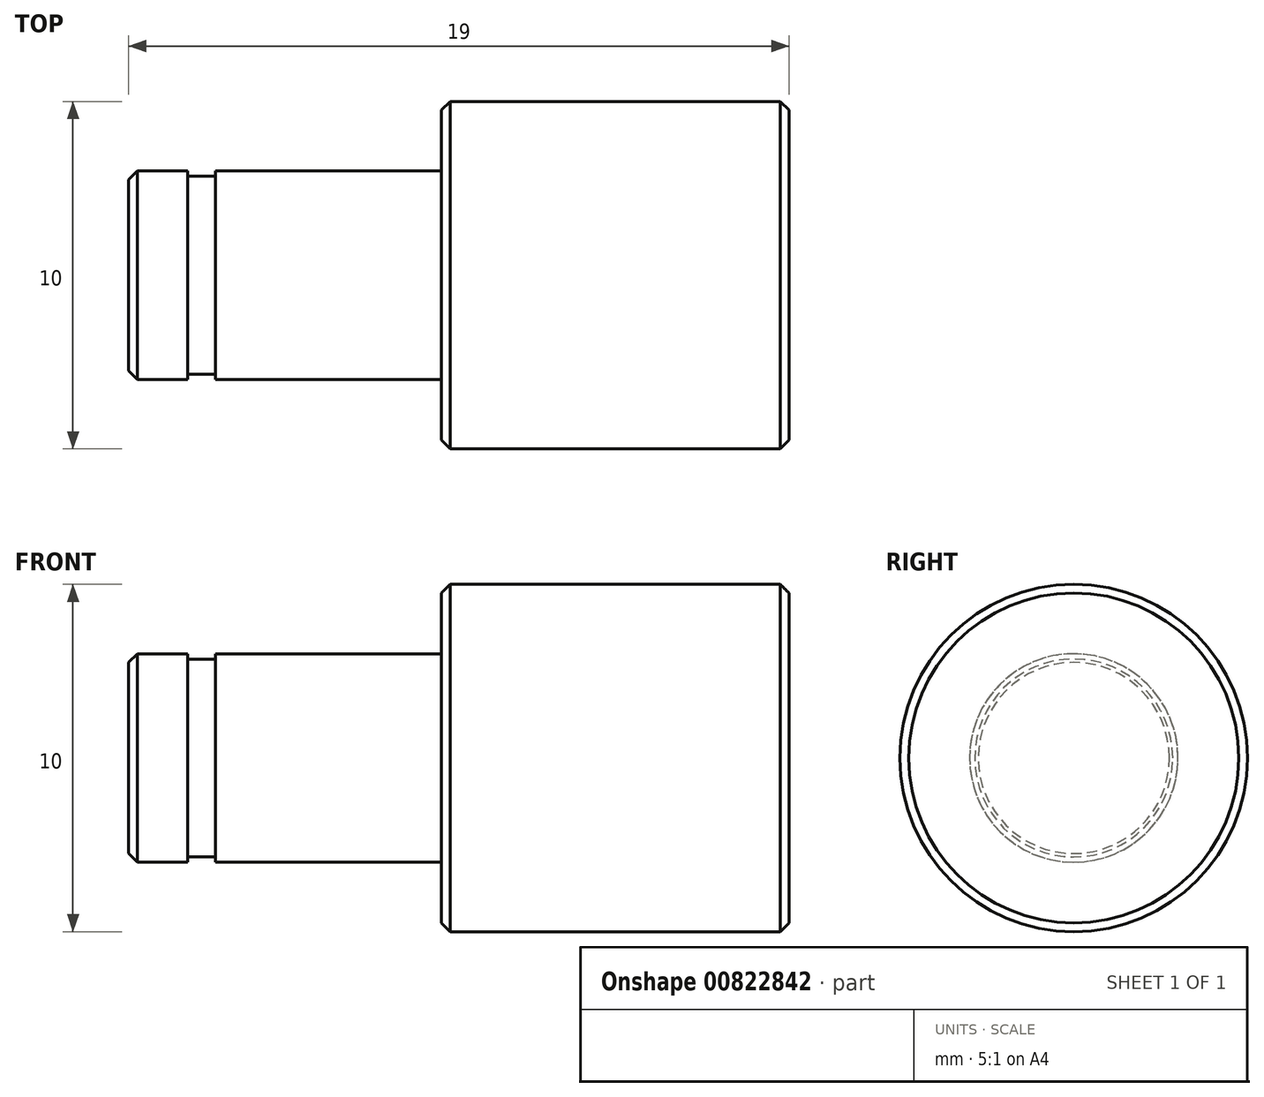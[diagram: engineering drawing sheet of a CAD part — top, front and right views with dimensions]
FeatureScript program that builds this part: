
annotation { "Feature Type Name" : "Feature", "Feature Type Description" : "" }
export const myFeature = defineFeature(function(context is Context, id is Id, definition is map)
    precondition{}
    {
        {
            var Q0;
            Q0=qCreatedBy(makeId("Front.planeOp"),FACE);
            var sketch = newSketch(context, id + "F0", { "sketchPlane" : qUnion([Q0])});
            skLineSegment(sketch, "E0", {"start": v(0, 0) * mm, "end": v(0, 5) * mm});
            skLineSegment(sketch, "E1", {"start": v(0, 5) * mm, "end": v(-10, 5) * mm});
            skLineSegment(sketch, "E2", {"start": v(-19, 3) * mm, "end": v(-19, 0) * mm});
            skLineSegment(sketch, "E3", {"start": v(-19, 0) * mm, "end": v(0, 0) * mm});
            skLineSegment(sketch, "E4", {"start": v(0, 0) * mm, "end": v(12.92, 0) * mm, "construction": true});
            skLineSegment(sketch, "E5", {"start": v(-16.5, 3) * mm, "end": v(-10, 3) * mm});
            skLineSegment(sketch, "E6", {"start": v(-10, 3) * mm, "end": v(-10, 5) * mm});
            skPoint(sketch, "E7.orphan", {"position": v(-16.5, 5) * mm});
            skPoint(sketch, "E8.end.orphan", {"position": v(-18.68, 5) * mm});
            skLineSegment(sketch, "E9", {"start": v(-19, 3) * mm, "end": v(-17.3, 3) * mm});
            skLineSegment(sketch, "E10", {"start": v(-17.3, 3) * mm, "end": v(-17.3, 2.85) * mm});
            skLineSegment(sketch, "E11", {"start": v(-16.5, 3) * mm, "end": v(-16.5, 2.85) * mm});
            skLineSegment(sketch, "E12", {"start": v(-16.5, 2.85) * mm, "end": v(-17.3, 2.85) * mm});
            skSolve(sketch);
        }
        {
            var Q0;
            Q0=makeQuery(id+"F0.imprint","IMPRINT",FACE,{"disambiguationData":[TD([[makeQuery(id+"F0.imprint","IMPRINT",EDGE,{"derivedFrom":sQuery(id+"F0.wireOp",EDGE,"E0")}),1.0]])]});
            var Q1;
            Q1=sQuery(id+"F0.wireOp",EDGE,"E4");
            revolve(context, id + "F1", {"surfaceOperationType" : NewSurfaceOperationType.NEW, "entities" : qUnion([Q0]), "axis" : qUnion([Q1]), "revolveType" : RevolveType.FULL});
        }
        {
            var Q0;
            Q0=makeQuery(id+"F1.opRevolve","SWEPT_FACE",FACE,{"disambiguationData":[OSD([sQuery(id+"F0.wireOp",EDGE,"E1")])]});
            var Q1;
            Q1=makeQuery(id+"F1.opRevolve","SWEPT_FACE",FACE,{"disambiguationData":[OSD([sQuery(id+"F0.wireOp",EDGE,"E2")])]});
            chamfer(context, id + "F2", {"entities" : qUnion([Q0, Q1]), "width" : 0.25 * mm, "tangentPropagation" : true});
        }
    });
